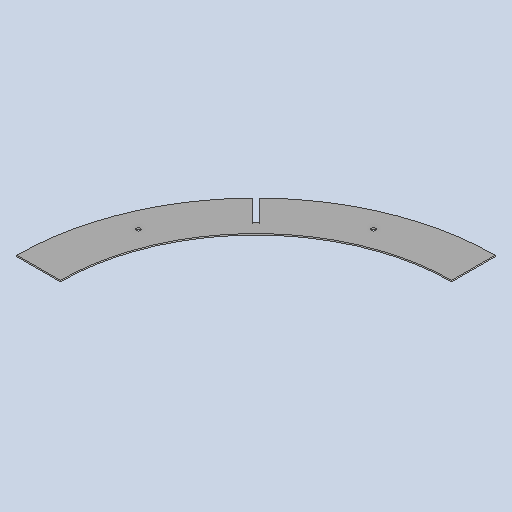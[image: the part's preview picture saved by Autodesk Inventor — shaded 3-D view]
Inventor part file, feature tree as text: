
AUTODESK INVENTOR PART (.ipt)
format: ipt  version: 2025 (Build 290162010, 162A)  size: 147,456 bytes
history: native  units: mm
features: other x4, sketch x3, sheet_metal_op x1, pattern_circular x1, extrude x1
ambient origin geometry x8: Origin, YZ Plane, XZ Plane, XY Plane, X Axis, Y Axis, Z Axis, Center Point
bodies: Solid1 (feature_tree)
feature tree (10):
  other  "BSH 502 segment"
  sheet_metal_op  "Face1"
  pattern_circular  "Circular Pattern1"  Count=110  [1 undecoded]
  extrude  "Extrusion1"  Depth=3.0mm
  sketch  "Sketch1"  dims[d1=900.0mm d2=3.0mm]
  other  "Plate1"
  sketch  "Sketch2"  dims[d4=10.0mm]
  sketch  "Sketch3"  dims[d5=22.5deg d6=3.0mm d7=0.0mm d8=20.0mm d9=45.0deg d11=45.0deg d12=12.0mm d13=70.0mm d14=0.0mm d15=0.0mm]
  other  "Cut1"
  other  "Definition1"
note: 1 required parameter value undecoded (feature->parameter linkage not recoverable at this tier; creation-order binding heuristic only, values carry confidence <= 0.55)
